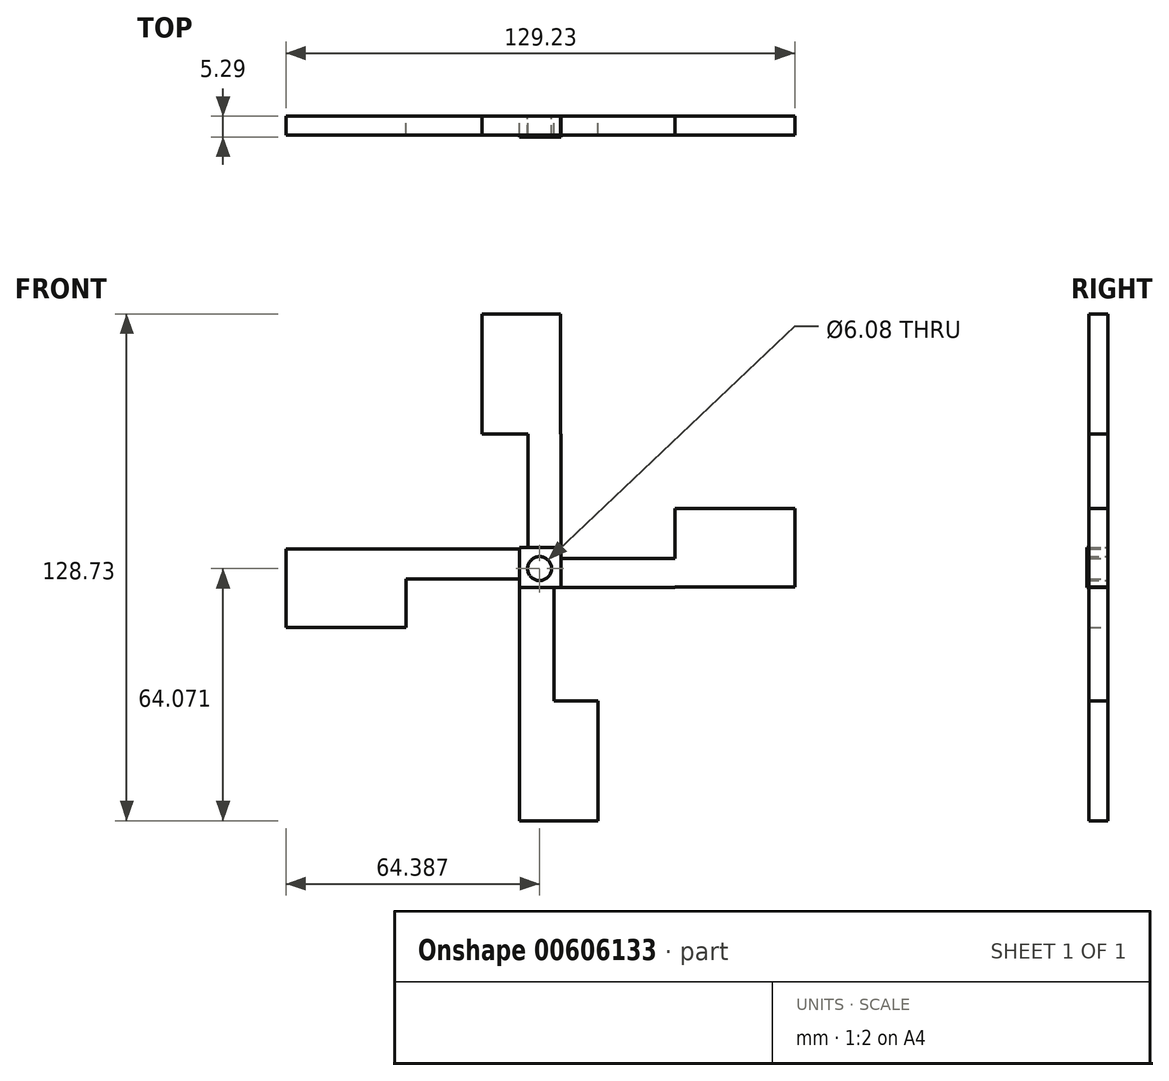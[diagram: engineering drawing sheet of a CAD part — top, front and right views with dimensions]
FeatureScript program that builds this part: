
annotation { "Feature Type Name" : "Feature", "Feature Type Description" : "" }
export const myFeature = defineFeature(function(context is Context, id is Id, definition is map)
    precondition{}
    {
        {
            var Q0;
            Q0=qCreatedBy(makeId("Front.planeOp"),FACE);
            var sketch = newSketch(context, id + "F0", { "sketchPlane" : qUnion([Q0])});
            skLineSegment(sketch, "E0.bottom", {"start": v(0, 0) * mm, "end": v(10.54, 0) * mm});
            skLineSegment(sketch, "E0.top", {"start": v(0, 10.1) * mm, "end": v(10.54, 10.1) * mm});
            skLineSegment(sketch, "E0.left", {"start": v(0, 0) * mm, "end": v(0, 10.1) * mm});
            skLineSegment(sketch, "E0.right", {"start": v(10.54, 0) * mm, "end": v(10.54, 10.1) * mm});
            skCircle(sketch, "E1", {"center": v(5.06, 4.74) * mm, "radius": 3.04 * mm});
            skSolve(sketch);
        }
        {
            var Q0;
            Q0=qCreatedBy(makeId("Front.planeOp"),FACE);
            var sketch = newSketch(context, id + "F1", { "sketchPlane" : qUnion([Q0])});
            skLineSegment(sketch, "E2.bottom", {"start": v(0, -28.85) * mm, "end": v(19.94, -28.85) * mm});
            skLineSegment(sketch, "E2.top", {"start": v(0, -59.33) * mm, "end": v(19.94, -59.33) * mm});
            skLineSegment(sketch, "E2.left", {"start": v(0, -28.85) * mm, "end": v(0, -59.33) * mm});
            skLineSegment(sketch, "E2.right", {"start": v(19.94, -28.85) * mm, "end": v(19.94, -59.33) * mm});
            skLineSegment(sketch, "E3.bottom", {"start": v(39.42, 20.01) * mm, "end": v(69.9, 20.01) * mm});
            skLineSegment(sketch, "E3.top", {"start": v(39.42, 0.08) * mm, "end": v(69.9, 0.08) * mm});
            skLineSegment(sketch, "E3.left", {"start": v(39.42, 20.01) * mm, "end": v(39.42, 0.08) * mm});
            skLineSegment(sketch, "E3.right", {"start": v(69.9, 20.01) * mm, "end": v(69.9, 0.08) * mm});
            skLineSegment(sketch, "E4.bottom", {"start": v(10.56, 0) * mm, "end": v(39.42, 0) * mm});
            skLineSegment(sketch, "E4.top", {"start": v(10.56, 7.32) * mm, "end": v(39.42, 7.32) * mm});
            skLineSegment(sketch, "E4.left", {"start": v(10.56, 0) * mm, "end": v(10.56, 7.32) * mm});
            skLineSegment(sketch, "E4.right", {"start": v(39.42, 0) * mm, "end": v(39.42, 7.32) * mm});
            skLineSegment(sketch, "E5.bottom", {"start": v(-28.85, 2.16) * mm, "end": v(0, 2.16) * mm});
            skLineSegment(sketch, "E5.top", {"start": v(-28.85, 9.68) * mm, "end": v(0, 9.68) * mm});
            skLineSegment(sketch, "E5.right", {"start": v(0, 2.16) * mm, "end": v(0, 9.68) * mm});
            skPoint(sketch, "E6.oppositeSnap0", {"position": v(9.97, -28.85) * mm});
            skLineSegment(sketch, "E6.bottom", {"start": v(0, -28.85) * mm, "end": v(9.97, -28.85) * mm});
            skLineSegment(sketch, "E6.top", {"start": v(0, 0) * mm, "end": v(9.97, 0) * mm});
            skLineSegment(sketch, "E6.left", {"start": v(0, -28.85) * mm, "end": v(0, 0) * mm});
            skLineSegment(sketch, "E7.bottom", {"start": v(-28.85, 9.68) * mm, "end": v(-59.33, 9.68) * mm});
            skLineSegment(sketch, "E7.top", {"start": v(-28.85, -10.26) * mm, "end": v(-59.33, -10.26) * mm});
            skLineSegment(sketch, "E7.left", {"start": v(-28.85, 9.68) * mm, "end": v(-28.85, -10.26) * mm});
            skLineSegment(sketch, "E7.right", {"start": v(-59.33, 9.68) * mm, "end": v(-59.33, -10.26) * mm});
            skLineSegment(sketch, "E8", {"start": v(10.54, 10.08) * mm, "end": v(10.54, 38.94) * mm});
            skLineSegment(sketch, "E9", {"start": v(2.1, 10.08) * mm, "end": v(2.1, 31.52) * mm});
            skLineSegment(sketch, "E10.bottom", {"start": v(-9.6, 38.92) * mm, "end": v(10.34, 38.92) * mm});
            skLineSegment(sketch, "E10.top", {"start": v(-9.6, 69.4) * mm, "end": v(10.34, 69.4) * mm});
            skLineSegment(sketch, "E10.left", {"start": v(-9.6, 38.92) * mm, "end": v(-9.6, 69.4) * mm});
            skLineSegment(sketch, "E10.right", {"start": v(10.34, 38.92) * mm, "end": v(10.34, 69.4) * mm});
            skLineSegment(sketch, "E11.bottom", {"start": v(2.1, 10.08) * mm, "end": v(10.54, 10.08) * mm});
            skLineSegment(sketch, "E11.top", {"start": v(2.1, 38.94) * mm, "end": v(10.54, 38.94) * mm});
            skLineSegment(sketch, "E11.left", {"start": v(2.1, 10.08) * mm, "end": v(2.1, 38.94) * mm});
            skLineSegment(sketch, "E12", {"start": v(8.72, 0) * mm, "end": v(8.72, -28.85) * mm});
            skSolve(sketch);
        }
        {
            var Q0;
            Q0=qSketchRegion(id+"F0",true);
            extrude(context, id + "F2", {"entities" : qUnion([Q0]), "depth" : 5.3 * mm});
        }
        {
            var Q0;
            Q0=qSketchRegion(id+"F1",true);
            extrude(context, id + "F3", {"entities" : qUnion([Q0]), "operationType" : NewBodyOperationType.ADD, "depth" : 4.76 * mm});
        }
    });
